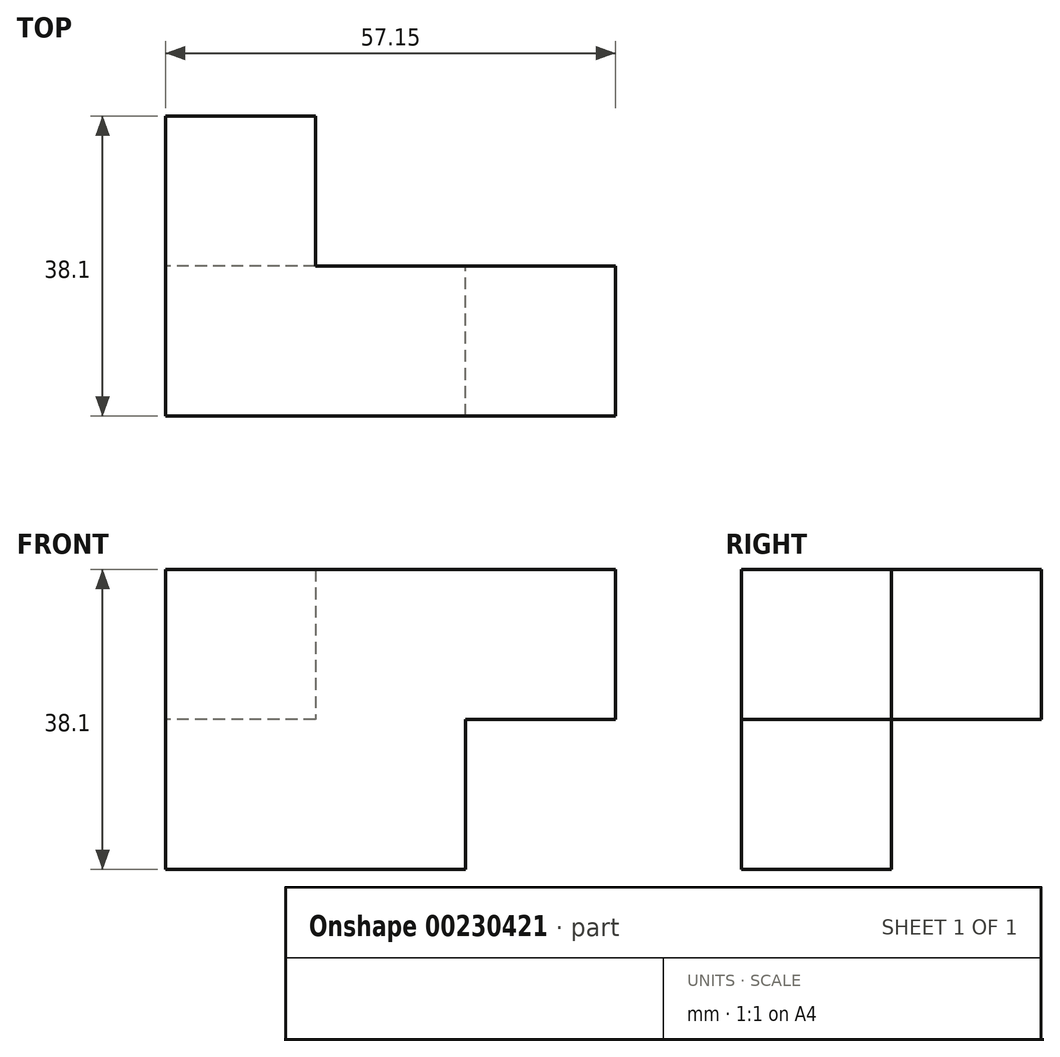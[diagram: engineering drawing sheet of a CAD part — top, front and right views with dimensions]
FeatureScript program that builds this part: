
annotation { "Feature Type Name" : "Feature", "Feature Type Description" : "" }
export const myFeature = defineFeature(function(context is Context, id is Id, definition is map)
    precondition{}
    {
        {
            var Q0;
            Q0=qCreatedBy(makeId("Front.planeOp"),FACE);
            var sketch = newSketch(context, id + "F0", { "sketchPlane" : qUnion([Q0])});
            skLineSegment(sketch, "E0.bottom", {"start": v(-86.89, 45) * mm, "end": v(-48.79, 45) * mm});
            skLineSegment(sketch, "E0.top", {"start": v(-86.89, 25.95) * mm, "end": v(-48.79, 25.95) * mm});
            skLineSegment(sketch, "E0.left", {"start": v(-86.89, 45) * mm, "end": v(-86.89, 25.95) * mm});
            skLineSegment(sketch, "E0.right", {"start": v(-48.79, 45) * mm, "end": v(-48.79, 25.95) * mm});
            skSolve(sketch);
        }
        {
            var Q0;
            Q0=makeQuery(id+"F0.imprint","IMPRINT",FACE,{"disambiguationData":[TD([[makeQuery(id+"F0.imprint","IMPRINT",EDGE,{"derivedFrom":sQuery(id+"F0.wireOp",EDGE,"E0.bottom")}),-1.0]])]});
            extrude(context, id + "F1", {"entities" : qUnion([Q0]), "depth" : 19.05 * mm});
        }
        {
            var Q0;
            Q0=makeQuery(id+"F1.opExtrude","SWEPT_FACE",FACE,{"disambiguationData":[OSD([sQuery(id+"F0.wireOp",EDGE,"E0.bottom")])]});
            var sketch = newSketch(context, id + "F2", { "sketchPlane" : qUnion([Q0])});
            skLineSegment(sketch, "E1.bottom", {"start": v(-86.89, 0) * mm, "end": v(-48.79, 0) * mm});
            skLineSegment(sketch, "E1.top", {"start": v(-86.89, -19.05) * mm, "end": v(-48.79, -19.05) * mm});
            skLineSegment(sketch, "E1.left", {"start": v(-86.89, 0) * mm, "end": v(-86.89, -19.05) * mm});
            skLineSegment(sketch, "E1.right", {"start": v(-48.79, 0) * mm, "end": v(-48.79, -19.05) * mm});
            skSolve(sketch);
        }
        {
            var Q0;
            Q0 = qSketchRegion(id + "F2", true);
            extrude(context, id + "F3", {"entities" : qUnion([Q0]), "operationType" : NewBodyOperationType.ADD, "depth" : 19.05 * mm});
        }
        {
            var Q0;
            Q0=makeQuery(id+"F3.boolean.opBoolean","MERGE",FACE,{"derivedFrom":[makeQuery(id+"F1.opExtrude","SWEPT_FACE",FACE,{"disambiguationData":[OSD([sQuery(id+"F0.wireOp",EDGE,"E0.right")])]}),makeQuery(id+"F3.opExtrude","SWEPT_FACE",FACE,{"disambiguationData":[OSD([sQuery(id+"F2.wireOp",EDGE,"E1.right")])]})]});
            var sketch = newSketch(context, id + "F4", { "sketchPlane" : qUnion([Q0])});
            skLineSegment(sketch, "E2.bottom", {"start": v(-19.05, 64.05) * mm, "end": v(0, 64.05) * mm});
            skLineSegment(sketch, "E2.top", {"start": v(-19.05, 45) * mm, "end": v(0, 45) * mm});
            skLineSegment(sketch, "E2.left", {"start": v(-19.05, 64.05) * mm, "end": v(-19.05, 45) * mm});
            skLineSegment(sketch, "E2.right", {"start": v(0, 64.05) * mm, "end": v(0, 45) * mm});
            skSolve(sketch);
        }
        {
            var Q0;
            Q0 = qSketchRegion(id + "F4", true);
            extrude(context, id + "F5", {"entities" : qUnion([Q0]), "operationType" : NewBodyOperationType.ADD, "depth" : 19.05 * mm});
        }
        {
            var Q0;
            Q0=makeQuery(id+"F5.boolean.opBoolean","MERGE",FACE,{"derivedFrom":[makeQuery(id+"F3.boolean.opBoolean","MERGE",FACE,{"derivedFrom":[makeQuery(id+"F1.opExtrude","CAP_FACE",FACE,{"disambiguationData":[OSD([sQuery(id+"F0.wireOp",EDGE,"E0.bottom"),sQuery(id+"F0.wireOp",EDGE,"E0.top"),sQuery(id+"F0.wireOp",EDGE,"E0.left"),sQuery(id+"F0.wireOp",EDGE,"E0.right")])],"isStart":true}),makeQuery(id+"F3.opExtrude","SWEPT_FACE",FACE,{"disambiguationData":[OSD([sQuery(id+"F2.wireOp",EDGE,"E1.bottom")])]})]}),makeQuery(id+"F5.opExtrude","SWEPT_FACE",FACE,{"disambiguationData":[OSD([sQuery(id+"F4.wireOp",EDGE,"E2.right")])]})]});
            var sketch = newSketch(context, id + "F6", { "sketchPlane" : qUnion([Q0])});
            skLineSegment(sketch, "E3.bottom", {"start": v(67.84, 64.05) * mm, "end": v(86.89, 64.05) * mm});
            skLineSegment(sketch, "E3.top", {"start": v(67.84, 45) * mm, "end": v(86.89, 45) * mm});
            skLineSegment(sketch, "E3.left", {"start": v(67.84, 64.05) * mm, "end": v(67.84, 45) * mm});
            skLineSegment(sketch, "E3.right", {"start": v(86.89, 64.05) * mm, "end": v(86.89, 45) * mm});
            skSolve(sketch);
        }
        {
            var Q0;
            Q0 = qSketchRegion(id + "F6", true);
            extrude(context, id + "F7", {"entities" : qUnion([Q0]), "operationType" : NewBodyOperationType.ADD, "depth" : 19.05 * mm});
        }
    });
